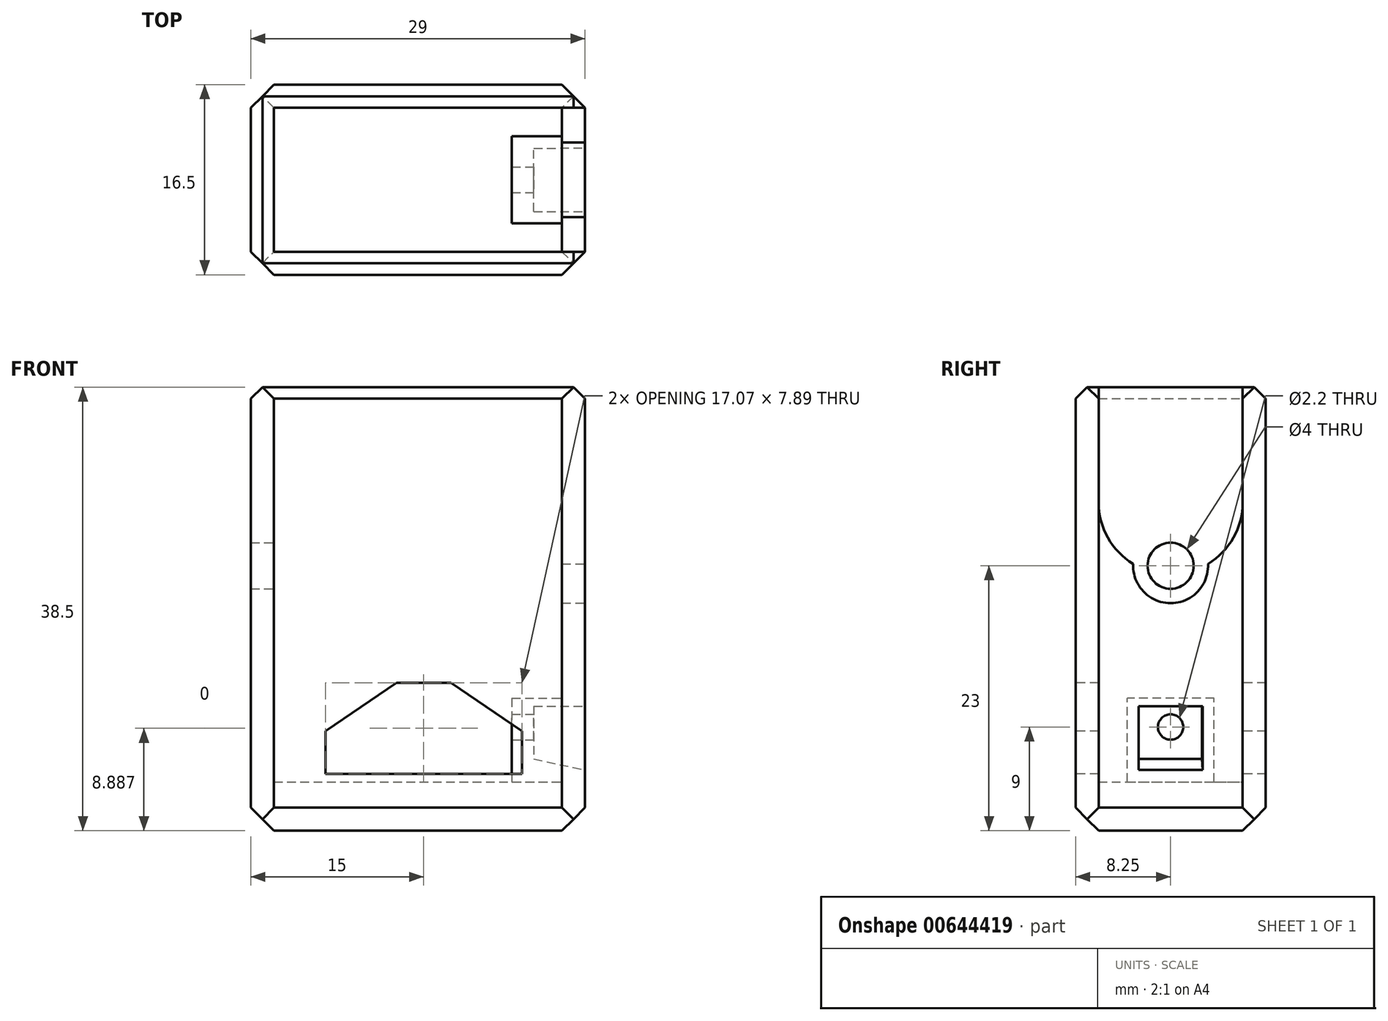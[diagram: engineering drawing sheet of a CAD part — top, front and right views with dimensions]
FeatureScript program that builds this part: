
annotation { "Feature Type Name" : "Feature", "Feature Type Description" : "" }
export const myFeature = defineFeature(function(context is Context, id is Id, definition is map)
    precondition{}
    {
        {
            var Q0;
            Q0=qCreatedBy(makeId("Top.planeOp"),FACE);
            var sketch = newSketch(context, id + "F0", { "sketchPlane" : qUnion([Q0])});
            skLineSegment(sketch, "E0.bottom", {"start": v(0, 0) * mm, "end": v(29, 0) * mm});
            skLineSegment(sketch, "E0.top", {"start": v(0, 16.5) * mm, "end": v(29, 16.5) * mm});
            skLineSegment(sketch, "E0.left", {"start": v(0, 0) * mm, "end": v(0, 16.5) * mm});
            skLineSegment(sketch, "E0.right", {"start": v(29, 0) * mm, "end": v(29, 16.5) * mm});
            skSolve(sketch);
        }
        {
            var Q0;
            Q0 = qSketchRegion(id + "F0", true);
            extrude(context, id + "F1", {"entities" : qUnion([Q0]), "depth" : 38.5 * mm, "offsetDistance" : 25 * mm});
        }
        {
            var Q0;
            Q0=makeQuery(id+"F1.opExtrude","CAP_FACE",FACE,{"disambiguationData":[OSD([sQuery(id+"F0.wireOp",EDGE,"E0.bottom"),sQuery(id+"F0.wireOp",EDGE,"E0.top"),sQuery(id+"F0.wireOp",EDGE,"E0.left"),sQuery(id+"F0.wireOp",EDGE,"E0.right")])],"isStart":false});
            shell(context, id + "F2", {"entities" : qUnion([Q0]), "thickness" : 2 * mm});
        }
        {
            var Q0;
            Q0=makeQuery(id+"F2.opShell","OFFSET_FACE",FACE,{"disambiguationData":[OSD([sQuery(id+"F0.wireOp",EDGE,"E0.bottom"),sQuery(id+"F0.wireOp",EDGE,"E0.top"),sQuery(id+"F0.wireOp",EDGE,"E0.left"),sQuery(id+"F0.wireOp",EDGE,"E0.right")])]});
            extrude(context, id + "F3", {"entities" : qUnion([Q0]), "operationType" : NewBodyOperationType.ADD, "depth" : 2.25 * mm, "offsetDistance" : 25 * mm});
        }
        {
            var Q0;
            Q0=makeQuery(id+"F1.opExtrude","SWEPT_EDGE",EDGE,{"disambiguationData":[OSD([sQuery(id+"F0.wireOp",EDGE,"E0.bottom"),sQuery(id+"F0.wireOp",EDGE,"E0.right")])]});
            var Q1;
            Q1=makeQuery(id+"F1.opExtrude","SWEPT_EDGE",EDGE,{"disambiguationData":[OSD([sQuery(id+"F0.wireOp",EDGE,"E0.top"),sQuery(id+"F0.wireOp",EDGE,"E0.right")])]});
            var Q2;
            Q2=makeQuery(id+"F1.opExtrude","SWEPT_EDGE",EDGE,{"disambiguationData":[OSD([sQuery(id+"F0.wireOp",EDGE,"E0.top"),sQuery(id+"F0.wireOp",EDGE,"E0.left")])]});
            var Q3;
            Q3=makeQuery(id+"F1.opExtrude","SWEPT_EDGE",EDGE,{"disambiguationData":[OSD([sQuery(id+"F0.wireOp",EDGE,"E0.bottom"),sQuery(id+"F0.wireOp",EDGE,"E0.left")])]});
            chamfer(context, id + "F4", {"entities" : qUnion([Q0, Q1, Q2, Q3]), "width" : 2 * mm, "tangentPropagation" : true});
        }
        {
            var Q0;
            Q0=makeQuery(id+"F1.opExtrude","CAP_EDGE",EDGE,{"disambiguationData":[OSD([sQuery(id+"F0.wireOp",EDGE,"E0.top")])],"isStart":true});
            var Q1;
            Q1=makeQuery(id+"F1.opExtrude","CAP_EDGE",EDGE,{"disambiguationData":[OSD([sQuery(id+"F0.wireOp",EDGE,"E0.left")])],"isStart":true});
            var Q2;
            Q2=makeQuery(id+"F1.opExtrude","CAP_EDGE",EDGE,{"disambiguationData":[OSD([sQuery(id+"F0.wireOp",EDGE,"E0.bottom")])],"isStart":true});
            var Q3;
            Q3=makeQuery(id+"F1.opExtrude","CAP_EDGE",EDGE,{"disambiguationData":[OSD([sQuery(id+"F0.wireOp",EDGE,"E0.right")])],"isStart":true});
            chamfer(context, id + "F5", {"entities" : qUnion([Q0, Q1, Q2, Q3]), "width" : 2 * mm, "tangentPropagation" : true});
        }
        {
            var Q0;
            Q0=makeQuery(id+"F1.opExtrude","CAP_EDGE",EDGE,{"disambiguationData":[OSD([sQuery(id+"F0.wireOp",EDGE,"E0.top")])],"isStart":false});
            var Q1;
            Q1=makeQuery(id+"F1.opExtrude","CAP_EDGE",EDGE,{"disambiguationData":[OSD([sQuery(id+"F0.wireOp",EDGE,"E0.left")])],"isStart":false});
            var Q2;
            Q2=makeQuery(id+"F1.opExtrude","CAP_EDGE",EDGE,{"disambiguationData":[OSD([sQuery(id+"F0.wireOp",EDGE,"E0.bottom")])],"isStart":false});
            var Q3;
            Q3=makeQuery(id+"F1.opExtrude","CAP_EDGE",EDGE,{"disambiguationData":[OSD([sQuery(id+"F0.wireOp",EDGE,"E0.right")])],"isStart":false});
            chamfer(context, id + "F6", {"entities" : qUnion([Q0, Q1, Q2, Q3]), "width" : 1 * mm, "tangentPropagation" : true});
        }
        {
            var Q0;
            Q0=makeQuery(id+"F1.opExtrude","SWEPT_FACE",FACE,{"disambiguationData":[OSD([sQuery(id+"F0.wireOp",EDGE,"E0.bottom")])]});
            var sketch = newSketch(context, id + "F7", { "sketchPlane" : qUnion([Q0])});
            skLineSegment(sketch, "E1", {"start": v(6.46, 4.94) * mm, "end": v(23.54, 4.94) * mm});
            skLineSegment(sketch, "E2", {"start": v(23.54, 4.94) * mm, "end": v(23.54, 8.66) * mm});
            skLineSegment(sketch, "E3", {"start": v(23.54, 8.66) * mm, "end": v(17.36, 12.83) * mm});
            skLineSegment(sketch, "E4", {"start": v(17.36, 12.83) * mm, "end": v(12.63, 12.83) * mm});
            skLineSegment(sketch, "E5", {"start": v(12.63, 12.83) * mm, "end": v(6.46, 8.66) * mm});
            skLineSegment(sketch, "E6", {"start": v(6.46, 8.66) * mm, "end": v(6.46, 4.94) * mm});
            skSolve(sketch);
        }
        {
            var Q0;
            Q0 = qSketchRegion(id + "F7", true);
            extrude(context, id + "F8", {"entities" : qUnion([Q0]), "operationType" : NewBodyOperationType.REMOVE, "endBound" : BoundingType.THROUGH_ALL, "oppositeDirection" : true, "depth" : 25 * mm, "offsetDistance" : 25 * mm});
        }
        {
            var Q0;
            Q0=makeQuery(id+"F1.opExtrude","SWEPT_FACE",FACE,{"disambiguationData":[OSD([sQuery(id+"F0.wireOp",EDGE,"E0.right")])]});
            var sketch = newSketch(context, id + "F9", { "sketchPlane" : qUnion([Q0])});
            skLineSegment(sketch, "E7.bottom", {"start": v(2, 38.5) * mm, "end": v(14.5, 38.5) * mm});
            skLineSegment(sketch, "E7.top", {"start": v(2, 28.5) * mm, "end": v(14.5, 28.5) * mm});
            skLineSegment(sketch, "E7.left", {"start": v(2, 38.5) * mm, "end": v(2, 28.5) * mm});
            skLineSegment(sketch, "E7.right", {"start": v(14.5, 38.5) * mm, "end": v(14.5, 28.5) * mm});
            skCircle(sketch, "E8", {"center": v(8.25, 28.5) * mm, "radius": 6.25 * mm});
            skCircle(sketch, "E9", {"center": v(8.25, 23) * mm, "radius": 3.25 * mm});
            skSolve(sketch);
        }
        {
            var Q0;
            Q0 = qSketchRegion(id + "F9", true);
            extrude(context, id + "F10", {"entities" : qUnion([Q0]), "operationType" : NewBodyOperationType.REMOVE, "endBound" : BoundingType.UP_TO_NEXT, "oppositeDirection" : true, "depth" : 25 * mm, "offsetDistance" : 25 * mm});
        }
        {
            var Q0;
            Q0=makeQuery(id+"F2.opShell","OFFSET_FACE",FACE,{"disambiguationData":[OSD([sQuery(id+"F0.wireOp",EDGE,"E0.left")])]});
            var sketch = newSketch(context, id + "F11", { "sketchPlane" : qUnion([Q0])});
            skCircle(sketch, "E10", {"center": v(8.25, 23) * mm, "radius": 2 * mm});
            skSolve(sketch);
        }
        {
            var Q0;
            Q0=makeQuery(id+"F11.imprint","IMPRINT",FACE,{"disambiguationData":[TD([[makeQuery(id+"F11.imprint","IMPRINT",EDGE,{"derivedFrom":sQuery(id+"F11.wireOp",EDGE,"E10")}),1.0]])]});
            extrude(context, id + "F12", {"entities" : qUnion([Q0]), "operationType" : NewBodyOperationType.REMOVE, "endBound" : BoundingType.THROUGH_ALL, "oppositeDirection" : true, "depth" : 25 * mm, "offsetDistance" : 25 * mm});
        }
        {
            var Q0;
            Q0=makeQuery(id+"F1.opExtrude","SWEPT_FACE",FACE,{"disambiguationData":[OSD([sQuery(id+"F0.wireOp",EDGE,"E0.right")])]});
            var sketch = newSketch(context, id + "F13", { "sketchPlane" : qUnion([Q0])});
            skLineSegment(sketch, "E11.bottom", {"start": v(4.48, 11.5) * mm, "end": v(12.02, 11.5) * mm});
            skLineSegment(sketch, "E11.top", {"start": v(4.48, 4.25) * mm, "end": v(12.02, 4.25) * mm});
            skLineSegment(sketch, "E11.left", {"start": v(4.48, 11.5) * mm, "end": v(4.48, 4.25) * mm});
            skLineSegment(sketch, "E11.right", {"start": v(12.02, 11.5) * mm, "end": v(12.02, 4.25) * mm});
            skCircle(sketch, "E12", {"center": v(8.25, 9) * mm, "radius": 1.1 * mm});
            skSolve(sketch);
        }
        {
            var Q0;
            Q0=makeQuery(id+"F13.imprint","IMPRINT",FACE,{"disambiguationData":[TD([[makeQuery(id+"F13.imprint","IMPRINT",EDGE,{"derivedFrom":sQuery(id+"F13.wireOp",EDGE,"E11.bottom")}),-1.0]])]});
            extrude(context, id + "F14", {"entities" : qUnion([Q0]), "operationType" : NewBodyOperationType.ADD, "depth" : -6.35 * mm, "offsetDistance" : 25 * mm});
        }
        {
            var Q0;
            Q0=makeQuery(id+"F1.opExtrude","SWEPT_FACE",FACE,{"disambiguationData":[OSD([sQuery(id+"F0.wireOp",EDGE,"E0.right")])]});
            var sketch = newSketch(context, id + "F15", { "sketchPlane" : qUnion([Q0])});
            skLineSegment(sketch, "E13.bottom", {"start": v(5.48, 10.8) * mm, "end": v(11.02, 10.8) * mm});
            skLineSegment(sketch, "E13.top", {"start": v(5.48, 5.27) * mm, "end": v(11.02, 5.27) * mm});
            skLineSegment(sketch, "E13.left", {"start": v(5.48, 10.8) * mm, "end": v(5.48, 5.27) * mm});
            skLineSegment(sketch, "E13.right", {"start": v(11.02, 10.8) * mm, "end": v(11.02, 5.27) * mm});
            skSolve(sketch);
        }
        {
            var Q0;
            Q0=makeQuery(id+"F15.imprint","IMPRINT",FACE,{"disambiguationData":[TD([[makeQuery(id+"F15.imprint","IMPRINT",EDGE,{"derivedFrom":sQuery(id+"F15.wireOp",EDGE,"E13.bottom")}),1.0]])]});
            cPlane(context, id + "F16", {"entities" : qUnion([Q0]), "cplaneType" : CPlaneType.OFFSET, "offset" : 4.45 * mm, "oppositeDirection" : true, "width" : 150 * mm, "height" : 150 * mm});
        }
        {
            var Q0;
            Q0=qCreatedBy(id+"F16.planeOp",FACE);
            var sketch = newSketch(context, id + "F17", { "sketchPlane" : qUnion([Q0])});
            skLineSegment(sketch, "E14.bottom", {"start": v(5.48, 10.8) * mm, "end": v(10.96, 10.8) * mm});
            skLineSegment(sketch, "E14.top", {"start": v(5.48, 6.22) * mm, "end": v(10.96, 6.22) * mm});
            skLineSegment(sketch, "E14.left", {"start": v(5.48, 10.8) * mm, "end": v(5.48, 6.22) * mm});
            skLineSegment(sketch, "E14.right", {"start": v(10.96, 10.8) * mm, "end": v(10.96, 6.22) * mm});
            skSolve(sketch);
        }
        {
            var Q1;
            Q1 = qSketchRegion(id + "F17", true);
            var Q2;
            Q2 = qSketchRegion(id + "F15", true);
            loft(context, id + "F18", {"operationType" : NewBodyOperationType.REMOVE, "sheetProfilesArray" : [{ "sheetProfileEntities" : qUnion([Q1]) }, { "sheetProfileEntities" : qUnion([Q2]) }]});
        }
    });
